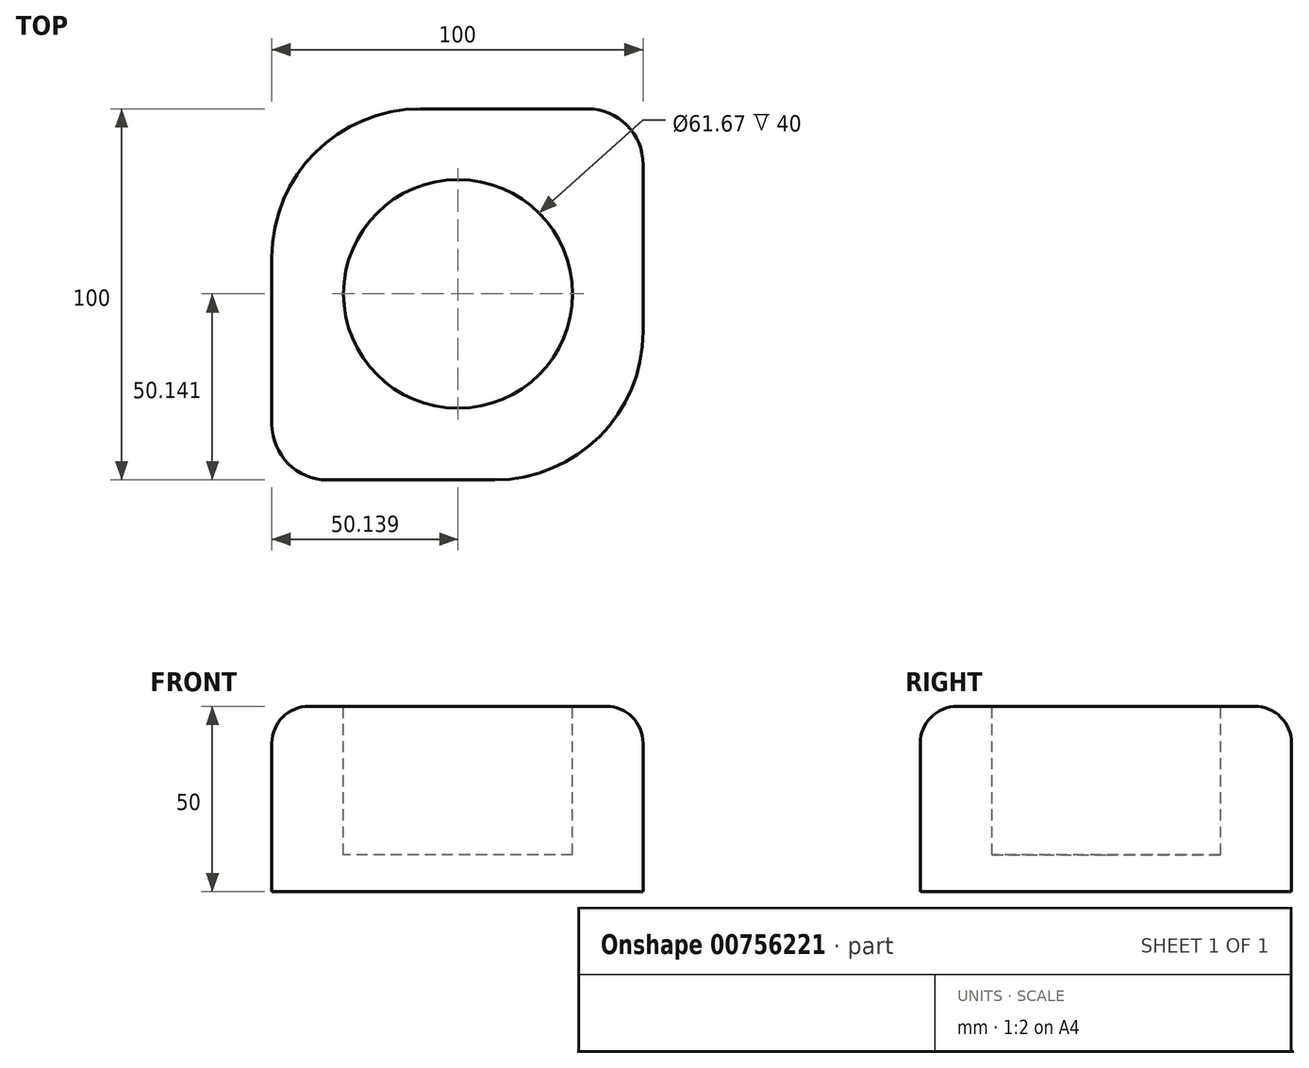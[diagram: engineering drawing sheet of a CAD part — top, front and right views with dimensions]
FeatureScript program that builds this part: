
annotation { "Feature Type Name" : "Feature", "Feature Type Description" : "" }
export const myFeature = defineFeature(function(context is Context, id is Id, definition is map)
    precondition{}
    {
        {
            var Q0;
            Q0=qCreatedBy(makeId("Top.planeOp"),FACE);
            var sketch = newSketch(context, id + "F0", { "sketchPlane" : qUnion([Q0])});
            skLineSegment(sketch, "E0.bottom", {"start": v(33.01, -64.82) * mm, "end": v(-66.99, -64.82) * mm});
            skLineSegment(sketch, "E0.top", {"start": v(33.01, 35.18) * mm, "end": v(-66.99, 35.18) * mm});
            skLineSegment(sketch, "E0.left", {"start": v(33.01, -64.82) * mm, "end": v(33.01, 35.18) * mm});
            skLineSegment(sketch, "E0.right", {"start": v(-66.99, -64.82) * mm, "end": v(-66.99, 35.18) * mm});
            skSolve(sketch);
        }
        {
            var Q0;
            Q0 = qSketchRegion(id + "F0", true);
            extrude(context, id + "F1", {"entities" : qUnion([Q0]), "depth" : 50 * mm, "offsetDistance" : 25 * mm});
        }
        {
            var Q0;
            Q0=makeQuery(id+"F1.opExtrude","CAP_EDGE",EDGE,{"disambiguationData":[OSD([sQuery(id+"F0.wireOp",EDGE,"E0.bottom")])],"isStart":false});
            var Q1;
            Q1=makeQuery(id+"F1.opExtrude","CAP_EDGE",EDGE,{"disambiguationData":[OSD([sQuery(id+"F0.wireOp",EDGE,"E0.left")])],"isStart":false});
            var Q2;
            Q2=makeQuery(id+"F1.opExtrude","CAP_EDGE",EDGE,{"disambiguationData":[OSD([sQuery(id+"F0.wireOp",EDGE,"E0.top")])],"isStart":false});
            var Q3;
            Q3=makeQuery(id+"F1.opExtrude","CAP_EDGE",EDGE,{"disambiguationData":[OSD([sQuery(id+"F0.wireOp",EDGE,"E0.right")])],"isStart":false});
            fillet(context, id + "F2", {"entities" : qUnion([Q0, Q1, Q2, Q3]), "radius" : 10 * mm, "tangentPropagation" : true, "allowEdgeOverflow" : false});
        }
        {
            var Q0;
            Q0=makeQuery(id+"F1.opExtrude","SWEPT_EDGE",EDGE,{"disambiguationData":[OSD([sQuery(id+"F0.wireOp",EDGE,"E0.bottom"),sQuery(id+"F0.wireOp",EDGE,"E0.left")])]});
            var Q1;
            Q1=makeQuery(id+"F2.opFillet","BLEND_EDGE",EDGE,{"blendedFrom":[makeQuery(id+"F1.opExtrude","CAP_EDGE",EDGE,{"disambiguationData":[OSD([sQuery(id+"F0.wireOp",EDGE,"E0.top")])],"isStart":false}),makeQuery(id+"F1.opExtrude","CAP_EDGE",EDGE,{"disambiguationData":[OSD([sQuery(id+"F0.wireOp",EDGE,"E0.right")])],"isStart":false})],"blendedInto":[]});
            fillet(context, id + "F3", {"entities" : qUnion([Q0, Q1]), "radius" : 40 * mm, "tangentPropagation" : true, "allowEdgeOverflow" : false});
        }
        {
            var Q0;
            Q0=makeQuery(id+"F1.opExtrude","SWEPT_EDGE",EDGE,{"disambiguationData":[OSD([sQuery(id+"F0.wireOp",EDGE,"E0.top"),sQuery(id+"F0.wireOp",EDGE,"E0.left")])]});
            var Q1;
            Q1=makeQuery(id+"F1.opExtrude","SWEPT_EDGE",EDGE,{"disambiguationData":[OSD([sQuery(id+"F0.wireOp",EDGE,"E0.bottom"),sQuery(id+"F0.wireOp",EDGE,"E0.right")])]});
            fillet(context, id + "F4", {"entities" : qUnion([Q0, Q1]), "radius" : 15 * mm, "tangentPropagation" : true, "allowEdgeOverflow" : false});
        }
        {
            var Q0;
            Q0=makeQuery(id+"F1.opExtrude","CAP_FACE",FACE,{"disambiguationData":[OSD([sQuery(id+"F0.wireOp",EDGE,"E0.bottom"),sQuery(id+"F0.wireOp",EDGE,"E0.top"),sQuery(id+"F0.wireOp",EDGE,"E0.left"),sQuery(id+"F0.wireOp",EDGE,"E0.right")])],"isStart":false});
            var sketch = newSketch(context, id + "F5", { "sketchPlane" : qUnion([Q0])});
            skCircle(sketch, "E1", {"center": v(-16.85, -14.68) * mm, "radius": 30.83 * mm});
            skSolve(sketch);
        }
        {
            var Q0;
            Q0=makeQuery(id+"F5.imprint","IMPRINT",FACE,{"disambiguationData":[TD([[makeQuery(id+"F5.imprint","IMPRINT",EDGE,{"derivedFrom":sQuery(id+"F5.wireOp",EDGE,"E1")}),1.0]])]});
            extrude(context, id + "F6", {"entities" : qUnion([Q0]), "operationType" : NewBodyOperationType.REMOVE, "oppositeDirection" : true, "depth" : 40 * mm, "offsetDistance" : 25 * mm});
        }
    });
